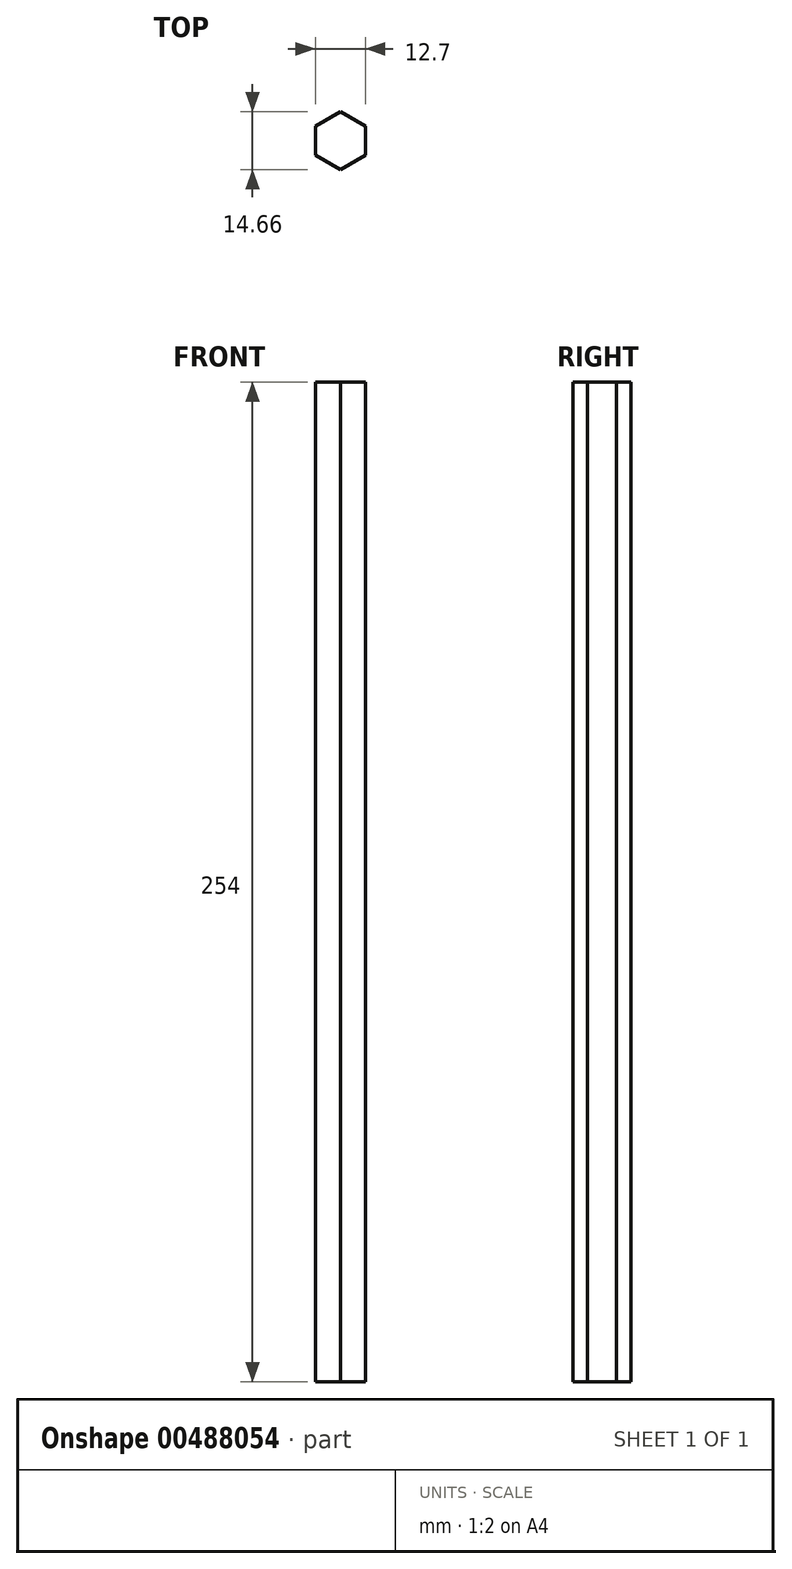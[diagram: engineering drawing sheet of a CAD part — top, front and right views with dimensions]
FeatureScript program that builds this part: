
annotation { "Feature Type Name" : "Feature", "Feature Type Description" : "" }
export const myFeature = defineFeature(function(context is Context, id is Id, definition is map)
    precondition{}
    {
        {
            var Q0;
            Q0=qCreatedBy(makeId("Top.planeOp"),FACE);
            var sketch = newSketch(context, id + "F0", { "sketchPlane" : qUnion([Q0])});
            skCircle(sketch, "E0.cCircle", {"center": v(0, 0) * mm, "radius": 6.35 * mm, "construction": true});
            skLineSegment(sketch, "E0.0", {"start": v(6.35, 3.67) * mm, "end": v(6.35, -3.67) * mm});
            skLineSegment(sketch, "E0.1", {"start": v(6.35, -3.67) * mm, "end": v(0, -7.33) * mm});
            skLineSegment(sketch, "E0.2", {"start": v(0, -7.33) * mm, "end": v(-6.35, -3.67) * mm});
            skLineSegment(sketch, "E0.3", {"start": v(-6.35, -3.67) * mm, "end": v(-6.35, 3.67) * mm});
            skLineSegment(sketch, "E0.4", {"start": v(-6.35, 3.67) * mm, "end": v(0, 7.33) * mm});
            skLineSegment(sketch, "E0.5", {"start": v(0, 7.33) * mm, "end": v(6.35, 3.67) * mm});
            skPoint(sketch, "E0.0.midPoint", {"position": v(6.35, 0) * mm});
            skSolve(sketch);
        }
        {
            var Q0;
            Q0=makeQuery(id+"F0.imprint","IMPRINT",FACE,{"disambiguationData":[TD([[makeQuery(id+"F0.imprint","IMPRINT",EDGE,{"derivedFrom":sQuery(id+"F0.wireOp",EDGE,"E0.0")}),-1.0]])]});
            extrude(context, id + "F1", {"entities" : qUnion([Q0]), "depth" : 254 * mm});
        }
    });
